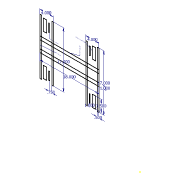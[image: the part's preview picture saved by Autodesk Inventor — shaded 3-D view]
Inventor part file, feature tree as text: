
AUTODESK INVENTOR PART (.ipt)
format: ipt  version: 2019 (Build 230136000, 136)  size: 124,928 bytes
history: native  units: in
note: dims shown in document units (in); Inventor stores cm internally (conversion verified against a paired STEP export)
features: other x5, sketch x3
ambient origin geometry x8: Origin, YZ Plane, XZ Plane, XY Plane, X Axis, Y Axis, Z Axis, Center Point
feature tree (8):
  other  "Annotations"
  sketch  "Sketch1"  dims[d0=0.5in]
  sketch  "Sketch10"  dims[d1=17.0in]
  sketch  "Sketch11"  dims[d8=4.0in d9=4.0in d12=3.5in d45=0.75in d52=17.0in d59=18.0in d60=1.0in d65=1.0in d69=0.2147in d70=0.2058in d71=0.2504in d72=0.1981in]
  other  "Leader Text 2"
  other  "Leader Text 3"
  other  "Leader Text 4"
  other  "Leader Text 5"
